# Revit family: 80010000
name_source: partatom
category: Plumbing Fixtures
revit_build: Autodesk Revit 2018 (Build: 20170223_1515(x64)
units: mm (PartAtom-declared; Revit-internal decimal feet)

## family parameters
Always vertical = Yes
Cut with Voids When Loaded = No
OmniClass Number = 23.45.55.00
OmniClass Title = Sanitary Faucets, Wastes
Part Type = Normal
Room Calculation Point = No
Round Connector Dimension = Use Diameter
Shared = No
Work Plane-Based = No

## types (1)
- 80010000 Body for bath and shower faucet, G3/4
    2D/3D/BIM Files URL = http://static.hansa.com
    3D View = https://static.hansa.com
    Additional Features = For the complete faucet, please order this concealed unit and a functional unit with the trim kit
    Advanced Features = Inner body made of DZR brass
    AssetType = Fixed
    BIMObjectName = 80010000
    Baseunit1NominalDepth = 76 mm
    Baseunit1NominalHeight = 168 mm  [stored 0.551181 ft]
    Baseunit1NominalWidth = 168 mm  [stored 0.551181 ft]
    Baseunit2NominalDepth = 59 mm
    Baseunit2NominalHeight = 123 mm
    Baseunit2NominalWidth = 123 mm
    BaseunitMainMaterial = Fine Textured - Gray
    Brand = HANSA
    Catalog Drawing URL = http://static.hansa.com
    Category = Bathroom;Shower;Public & Semi-public;Health & Care
    CloseOffRating = 0
    Color = Grey
    Concealed Parts = Gasket sleeve for dry mortarless construction;Mounting box and cover sleeve;Multifix fastening system
    Connection = Internal thread;with integrated shut-off valve(s)
    Connection Size = G3/4
    Dimension Drawing URL = http://static.hansa.com
    DurationUnit = Year
    EAN Number = 4015474279476
    ETIM Class Number = EC011327 Built-in mixing tap
    Excluded Items = Without trim kit
    FDV Document URL = http://www.hansa.com
    Features = Concealed unit
    FlowCoefficient = 0
    Group = Bath and shower faucet
    HWFU = 0
    IfcExportAs = IfcValveType
    IfcExportType = FAUCET
    InletConnectionSize = 20 mm  [stored 0.0656168 ft]
    Installation Depth = 75 - 105 mm
    Installation Type = Concealed wall mounting
    Installation and Maintenance Guide URL = http://static.hansa.com
    Interactive AR View URL = https://static.hansa.com
    Manufacturer = HANSA
    ManufacturerName = HANSA
    ManufacturerURL = http://www.hansa.com
    Market = Austria;Belgium;Czech Republic;Germany;Spain;France;International;Italy;Netherlands;Slovakia
    Max. Hot Water Supply = 80 °C
    Mechanical Parts = Pressure plug
    Mobile Product Information URL = http://mpi.hansa.com
    Model = 80010000 Body for bath and shower faucet, G3/4
    ModelReference = 80010000
    NBSDescription = Water supply fittings for baths
    NBSReference = 45-35-70/315
    Name = 80010000 Body for bath and shower faucet, G3/4
    Name_en = 80010000 Body for bath and shower faucet, G3/4
    Product Code = 80010000
    Product Family = HANSABLUEBOX
    Product Image URL = http://static.hansa.com
    Product URL = http://static.hansa.com
    ProductInformation = Concealed installation unit without shut-off valves
    Revision = 4
    Sales Package dimensions (LxWxH) = 190 x 180 x 160
    Shape = Sculptured
    Size = Baseunit 1: 168x76,4x168 mm / Baseunit 2: 123,4x58,6x123,4 mm
    Spare-Part Information URL = http://static.hansa.com
    Technical DataSheet URL = http://www.hansa.com
    UNSPSC Class Number = 30181702 Faucet unit
    URL Declaration of Conformity = http://static.hansa.com
    URL REACH = http://static.hansa.com
    Uniclass2 = Pr_40_30_96_07
    Uniclass2015Description = Bath manual water supply sets
    Uniclass2015Reference = Pr_40_20_87_07
    Version = 4
    VersionDate = 01/07/2022
    Warranty Information URL = http://warranty.hansa.com
    WarrantyDescription = http://warranty.hansa.com
    WarrantyDurationUnit = Year
    Working Pressure = 100 - 1000 kPa
    WorkingPressure = 100 - 1000 kPa

note: [stored X ft] marks values corroborated as IEEE doubles in the binary element streams (Revit-internal decimal feet)

## geometry (parser evidence)
native form markers: Sweep x8
no freeform markers — native parametric forms only
